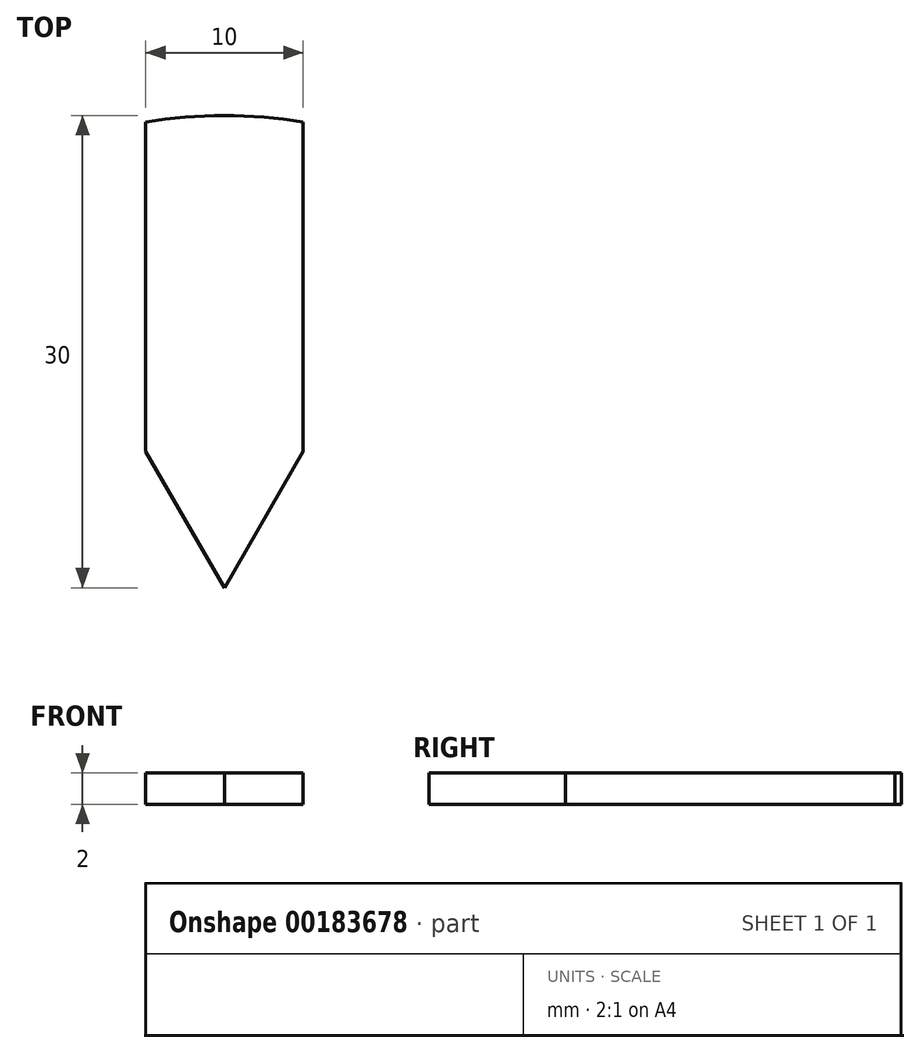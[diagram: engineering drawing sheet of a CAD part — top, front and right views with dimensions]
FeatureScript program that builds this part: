
annotation { "Feature Type Name" : "Feature", "Feature Type Description" : "" }
export const myFeature = defineFeature(function(context is Context, id is Id, definition is map)
    precondition{}
    {
        {
            var Q0;
            Q0=qCreatedBy(makeId("Top.planeOp"),FACE);
            var sketch = newSketch(context, id + "F0", { "sketchPlane" : qUnion([Q0])});
            skArc(sketch, "E0", {"start": v(5, 29.58) * mm, "mid": v(0, 30) * mm, "end": v(-5, 29.58) * mm});
            skLineSegment(sketch, "E1", {"start": v(-5, 29.58) * mm, "end": v(-5, 8.66) * mm});
            skLineSegment(sketch, "E2", {"start": v(-5, 8.66) * mm, "end": v(0, 0) * mm});
            skLineSegment(sketch, "E3", {"start": v(0, 0) * mm, "end": v(5, 8.66) * mm});
            skLineSegment(sketch, "E4", {"start": v(5, 8.66) * mm, "end": v(5, 29.58) * mm});
            skLineSegment(sketch, "E5", {"start": v(0, 30) * mm, "end": v(0, -10) * mm, "construction": true});
            skPoint(sketch, "E5.endSnap0", {"position": v(0, 30) * mm});
            skSolve(sketch);
        }
        {
            var Q0;
            Q0 = qSketchRegion(id + "F0", true);
            extrude(context, id + "F1", {"entities" : qUnion([Q0]), "depth" : 2 * mm});
        }
    });
